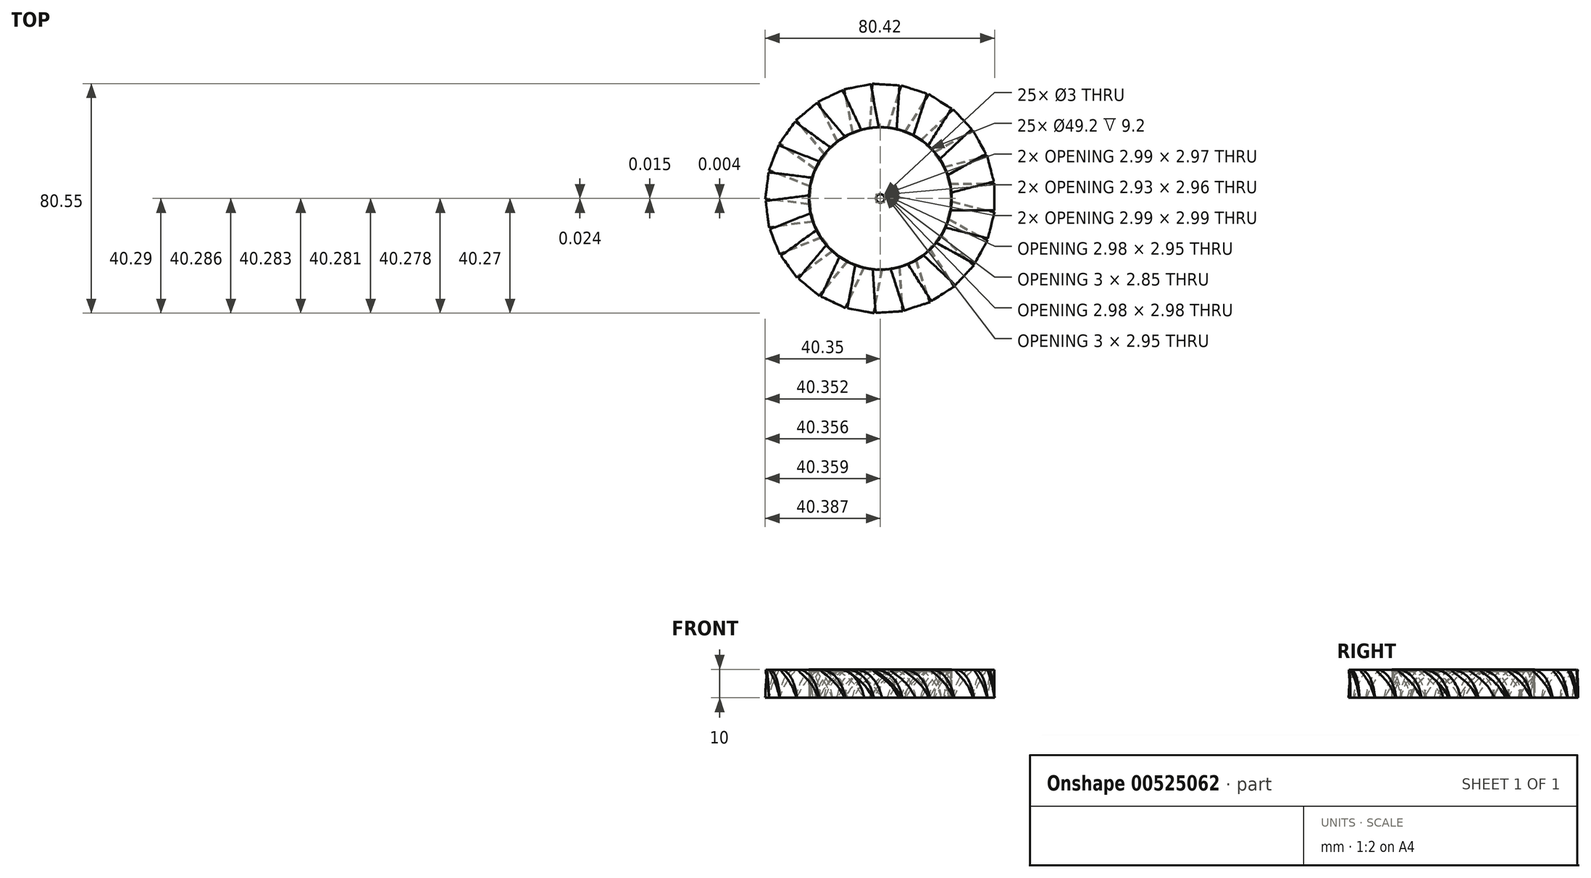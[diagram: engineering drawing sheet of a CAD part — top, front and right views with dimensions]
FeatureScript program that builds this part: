
annotation { "Feature Type Name" : "Feature", "Feature Type Description" : "" }
export const myFeature = defineFeature(function(context is Context, id is Id, definition is map)
    precondition{}
    {
        {
            var Q0;
            Q0=qCreatedBy(makeId("Top.planeOp"),FACE);
            var sketch = newSketch(context, id + "F0", { "sketchPlane" : qUnion([Q0])});
            skCircle(sketch, "E0", {"center": v(0, 0) * mm, "radius": 25 * mm});
            skCircle(sketch, "E1", {"center": v(0, 0) * mm, "radius": 1.5 * mm});
            skSolve(sketch);
        }
        {
            var Q0;
            Q0=qSketchRegion(id+"F0",true);
            extrude(context, id + "F1", {"entities" : qUnion([Q0]), "depth" : 10 * mm});
        }
        {
            var Q0;
            Q0=qCreatedBy(makeId("Right.planeOp"),FACE);
            cPlane(context, id + "F2", {"entities" : qUnion([Q0]), "cplaneType" : CPlaneType.OFFSET, "offset" : 40 * mm, "width" : 150 * mm, "height" : 150 * mm});
        }
        {
            var Q0;
            Q0=qCreatedBy(id+"F2.planeOp",FACE);
            var sketch = newSketch(context, id + "F3", { "sketchPlane" : qUnion([Q0])});
            skLineSegment(sketch, "E2", {"start": v(4.94, 0) * mm, "end": v(5.34, 0) * mm});
            skFitSpline(sketch, "E3", {"points": [v(5.34, 0) * mm, v(3.8, 4.27) * mm, v(0, 8.6) * mm, v(-4.2, 9.74) * mm, v(-1.78, 7.72) * mm, v(1.72, 4.7) * mm, v(4.94, 0) * mm], "startDerivative": vector(-19.2, 60.77) * mm, "endDerivative": vector(27.5, -47.99) * mm});
            skSolve(sketch);
        }
        {
            var Q0;
            Q0=qSketchRegion(id+"F3",true);
            extrude(context, id + "F4", {"entities" : qUnion([Q0]), "operationType" : NewBodyOperationType.ADD, "endBound" : BoundingType.UP_TO_NEXT, "oppositeDirection" : true, "depth" : 20 * mm});
        }
        {
            var Q0;
            Q0=makeQuery(id+"F1.opExtrude","SWEPT_BODY",BODY,{"disambiguationData":[OSD([sQuery(id+"F0.wireOp",EDGE,"E0"),sQuery(id+"F0.wireOp",EDGE,"E1")])]});
            var Q1;
            Q1=makeQuery(id+"F1.opExtrude","SWEPT_FACE",FACE,{"disambiguationData":[OSD([sQuery(id+"F0.wireOp",EDGE,"E0")])]});
            circularPattern(context, id + "F5", {"entities" : qUnion([Q0]), "axis" : qUnion([Q1]), "angle" : 360 * degree, "instanceCount" : 25, "equalSpace" : true});
        }
        {
            var Q0;
            Q0=makeQuery(id+"F4.boolean.opBoolean","MERGE",FACE,{"derivedFrom":[makeQuery(id+"F1.opExtrude","CAP_FACE",FACE,{"disambiguationData":[OSD([sQuery(id+"F0.wireOp",EDGE,"E0"),sQuery(id+"F0.wireOp",EDGE,"E1")])],"isStart":true}),makeQuery(id+"F4.opExtrude","SWEPT_FACE",FACE,{"disambiguationData":[OSD([sQuery(id+"F3.wireOp",EDGE,"E2")])]})]});
            var sketch = newSketch(context, id + "F6", { "sketchPlane" : qUnion([Q0])});
            skCircle(sketch, "E4", {"center": v(0, 0) * mm, "radius": 24.6 * mm});
            skSolve(sketch);
        }
        {
            var Q0;
            Q0=makeQuery(id+"F6.imprint","IMPRINT",FACE,{"disambiguationData":[TD([[makeQuery(id+"F6.imprint","IMPRINT",EDGE,{"derivedFrom":sQuery(id+"F6.wireOp",EDGE,"E4")}),1.0]])]});
            extrude(context, id + "F7", {"entities" : qUnion([Q0]), "operationType" : NewBodyOperationType.REMOVE, "oppositeDirection" : true, "depth" : 9.2 * mm});
        }
    });
